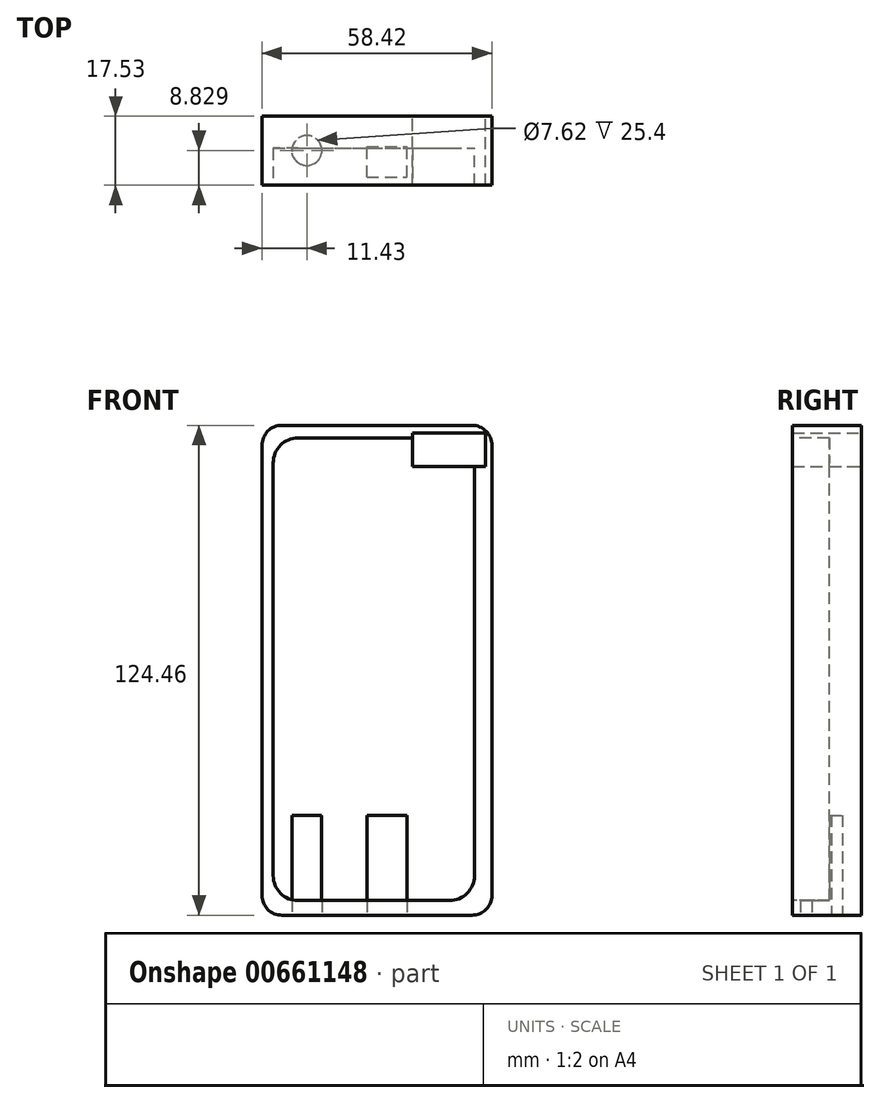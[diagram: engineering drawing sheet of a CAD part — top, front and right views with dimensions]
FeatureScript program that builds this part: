
annotation { "Feature Type Name" : "Feature", "Feature Type Description" : "" }
export const myFeature = defineFeature(function(context is Context, id is Id, definition is map)
    precondition{}
    {
        {
            var Q0;
            Q0=qCreatedBy(makeId("Front.planeOp"),FACE);
            var sketch = newSketch(context, id + "F0", { "sketchPlane" : qUnion([Q0])});
            skLineSegment(sketch, "E0.bottom", {"start": v(0, 0) * mm, "end": v(58.42, 0) * mm});
            skLineSegment(sketch, "E0.top", {"start": v(0, 124.46) * mm, "end": v(58.42, 124.46) * mm});
            skLineSegment(sketch, "E0.left", {"start": v(0, 0) * mm, "end": v(0, 124.46) * mm});
            skLineSegment(sketch, "E0.right", {"start": v(58.42, 0) * mm, "end": v(58.42, 124.46) * mm});
            skSolve(sketch);
        }
        {
            var Q0;
            Q0=makeQuery(id+"F0.imprint","IMPRINT",FACE,{"disambiguationData":[TD([[makeQuery(id+"F0.imprint","IMPRINT",EDGE,{"derivedFrom":sQuery(id+"F0.wireOp",EDGE,"E0.bottom")}),1.0]])]});
            extrude(context, id + "F1", {"entities" : qUnion([Q0]), "depth" : 17.53 * mm, "offsetDistance" : 25.4 * mm});
        }
        {
            var Q0;
            Q0=makeQuery(id+"F1.opExtrude","CAP_FACE",FACE,{"disambiguationData":[OSD([sQuery(id+"F0.wireOp",EDGE,"E0.bottom"),sQuery(id+"F0.wireOp",EDGE,"E0.top"),sQuery(id+"F0.wireOp",EDGE,"E0.left"),sQuery(id+"F0.wireOp",EDGE,"E0.right")])],"isStart":false});
            var sketch = newSketch(context, id + "F2", { "sketchPlane" : qUnion([Q0])});
            skLineSegment(sketch, "E1.bottom", {"start": v(9.21, 3.7) * mm, "end": v(47.66, 3.7) * mm});
            skLineSegment(sketch, "E1.top", {"start": v(9.21, 121.27) * mm, "end": v(47.66, 121.27) * mm});
            skLineSegment(sketch, "E1.left", {"start": v(2.86, 10.06) * mm, "end": v(2.86, 114.92) * mm});
            skLineSegment(sketch, "E1.right", {"start": v(54, 10.06) * mm, "end": v(54, 114.92) * mm});
            skPoint(sketch, "E2.visualSharp", {"position": v(2.86, 121.27) * mm});
            skArc(sketch, "E2.filletArc", {"start": v(9.21, 121.27) * mm, "mid": v(4.72, 119.41) * mm, "end": v(2.86, 114.92) * mm});
            skPoint(sketch, "E3.visualSharp", {"position": v(54, 121.27) * mm});
            skArc(sketch, "E3.filletArc", {"start": v(54, 114.92) * mm, "mid": v(52.15, 119.41) * mm, "end": v(47.66, 121.27) * mm});
            skPoint(sketch, "E4.visualSharp", {"position": v(54, 3.7) * mm});
            skArc(sketch, "E4.filletArc", {"start": v(47.66, 3.7) * mm, "mid": v(52.15, 5.57) * mm, "end": v(54, 10.06) * mm});
            skPoint(sketch, "E5.visualSharp", {"position": v(2.86, 3.7) * mm});
            skArc(sketch, "E5.filletArc", {"start": v(2.86, 10.06) * mm, "mid": v(4.72, 5.57) * mm, "end": v(9.21, 3.7) * mm});
            skSolve(sketch);
        }
        {
            var Q0;
            Q0=makeQuery(id+"F2.imprint","IMPRINT",FACE,{"disambiguationData":[TD([[makeQuery(id+"F2.imprint","IMPRINT",EDGE,{"derivedFrom":sQuery(id+"F2.wireOp",EDGE,"E1.bottom")}),1.0]])]});
            extrude(context, id + "F3", {"entities" : qUnion([Q0]), "operationType" : NewBodyOperationType.REMOVE, "oppositeDirection" : true, "depth" : 9.4 * mm, "offsetDistance" : 25.4 * mm});
        }
        {
            var Q0;
            Q0=qCreatedBy(makeId("Front.planeOp"),FACE);
            var sketch = newSketch(context, id + "F4", { "sketchPlane" : qUnion([Q0])});
            skLineSegment(sketch, "E6.bottom", {"start": v(56.77, 122.53) * mm, "end": v(38.32, 122.53) * mm});
            skLineSegment(sketch, "E6.top", {"start": v(56.77, 114.06) * mm, "end": v(38.32, 114.06) * mm});
            skLineSegment(sketch, "E6.left", {"start": v(56.77, 122.53) * mm, "end": v(56.77, 114.06) * mm});
            skLineSegment(sketch, "E6.right", {"start": v(38.32, 122.53) * mm, "end": v(38.32, 114.06) * mm});
            skSolve(sketch);
        }
        {
            var Q0;
            Q0=makeQuery(id+"F1.opExtrude","SWEPT_FACE",FACE,{"disambiguationData":[OSD([sQuery(id+"F0.wireOp",EDGE,"E0.bottom")])]});
            var sketch = newSketch(context, id + "F5", { "sketchPlane" : qUnion([Q0])});
            skCircle(sketch, "E7", {"center": v(11.43, 8.7) * mm, "radius": 3.81 * mm});
            skLineSegment(sketch, "E8.bottom", {"start": v(26.67, 15.5) * mm, "end": v(36.83, 15.5) * mm});
            skLineSegment(sketch, "E8.top", {"start": v(26.67, 7.69) * mm, "end": v(36.83, 7.69) * mm});
            skLineSegment(sketch, "E8.left", {"start": v(26.67, 15.5) * mm, "end": v(26.67, 7.69) * mm});
            skLineSegment(sketch, "E8.right", {"start": v(36.83, 15.5) * mm, "end": v(36.83, 7.69) * mm});
            skSolve(sketch);
        }
        {
            var Q0;
            Q0=makeQuery(id+"F1.opExtrude","SWEPT_EDGE",EDGE,{"disambiguationData":[OSD([sQuery(id+"F0.wireOp",EDGE,"E0.top"),sQuery(id+"F0.wireOp",EDGE,"E0.left")])]});
            var Q1;
            Q1=makeQuery(id+"F1.opExtrude","SWEPT_EDGE",EDGE,{"disambiguationData":[OSD([sQuery(id+"F0.wireOp",EDGE,"E0.top"),sQuery(id+"F0.wireOp",EDGE,"E0.right")])]});
            var Q2;
            Q2=makeQuery(id+"F1.opExtrude","SWEPT_EDGE",EDGE,{"disambiguationData":[OSD([sQuery(id+"F0.wireOp",EDGE,"E0.bottom"),sQuery(id+"F0.wireOp",EDGE,"E0.right")])]});
            var Q3;
            Q3=makeQuery(id+"F1.opExtrude","SWEPT_EDGE",EDGE,{"disambiguationData":[OSD([sQuery(id+"F0.wireOp",EDGE,"E0.bottom"),sQuery(id+"F0.wireOp",EDGE,"E0.left")])]});
            fillet(context, id + "F6", {"entities" : qUnion([Q0, Q1, Q2, Q3]), "radius" : 5.08 * mm, "tangentPropagation" : true, "allowEdgeOverflow" : false});
        }
        {
            var Q0;
            Q0=makeQuery(id+"F4.imprint","IMPRINT",FACE,{"disambiguationData":[TD([[makeQuery(id+"F4.imprint","IMPRINT",EDGE,{"derivedFrom":sQuery(id+"F4.wireOp",EDGE,"E6.bottom")}),1.0]])]});
            extrude(context, id + "F7", {"entities" : qUnion([Q0]), "operationType" : NewBodyOperationType.REMOVE, "depth" : 25.4 * mm, "offsetDistance" : 25.4 * mm});
        }
        {
            var Q0;
            Q0=makeQuery(id+"F5.imprint","IMPRINT",FACE,{"disambiguationData":[TD([[makeQuery(id+"F5.imprint","IMPRINT",EDGE,{"derivedFrom":sQuery(id+"F5.wireOp",EDGE,"E7")}),1.0]])]});
            var Q1;
            Q1=makeQuery(id+"F5.imprint","IMPRINT",FACE,{"disambiguationData":[TD([[makeQuery(id+"F5.imprint","IMPRINT",EDGE,{"derivedFrom":sQuery(id+"F5.wireOp",EDGE,"E8.bottom")}),-1.0]])]});
            extrude(context, id + "F8", {"entities" : qUnion([Q0, Q1]), "operationType" : NewBodyOperationType.REMOVE, "oppositeDirection" : true, "depth" : 25.4 * mm, "offsetDistance" : 25.4 * mm});
        }
    });
